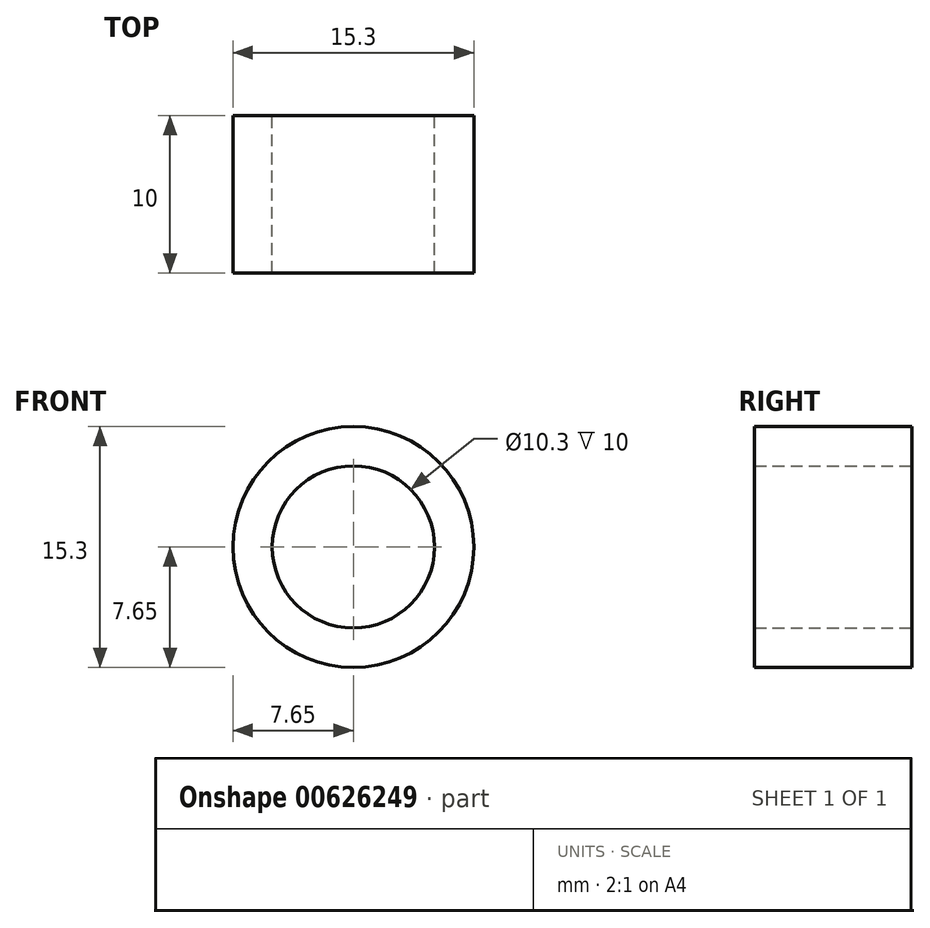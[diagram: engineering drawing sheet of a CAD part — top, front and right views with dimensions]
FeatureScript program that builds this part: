
annotation { "Feature Type Name" : "Feature", "Feature Type Description" : "" }
export const myFeature = defineFeature(function(context is Context, id is Id, definition is map)
    precondition{}
    {
        {
            var Q0;
            Q0=qCreatedBy(makeId("Front.planeOp"),FACE);
            var sketch = newSketch(context, id + "F0", { "sketchPlane" : qUnion([Q0])});
            skCircle(sketch, "E0", {"center": v(0, 0) * mm, "radius": 7.65 * mm});
            skCircle(sketch, "E1", {"center": v(0, 0) * mm, "radius": 5.15 * mm});
            skSolve(sketch);
        }
        {
            var Q0;
            Q0 = qSketchRegion(id + "F0", true);
            extrude(context, id + "F1", {"entities" : qUnion([Q0]), "depth" : 10 * mm, "offsetDistance" : 25 * mm});
        }
    });
